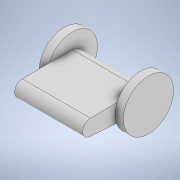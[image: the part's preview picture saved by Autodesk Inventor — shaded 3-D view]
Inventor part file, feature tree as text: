
AUTODESK INVENTOR PART (.ipt)
format: ipt  version: 2020 (Build 240168000, 168)  size: 137,728 bytes
history: native  units: mm
features: extrude x3, sketch x3, projected_geometry x2, other x1
ambient origin geometry x8: Origin, YZ Plane, XZ Plane, XY Plane, X Axis, Y Axis, Z Axis, Center Point
bodies: Body1 (feature_tree)
feature tree (9):
  other  "Твердое тело1"
  extrude  "Выдавливание1"  Depth=18.6mm
  extrude  "Выдавливание2"  Depth=12.2mm
  extrude  "Выдавливание3"  Depth=9.7mm
  sketch  "Эскиз1"
  sketch  "Эскиз2"
  projected_geometry  "Спроецированная петля1"
  sketch  "Эскиз3"
  projected_geometry  "Спроецированная петля2"
